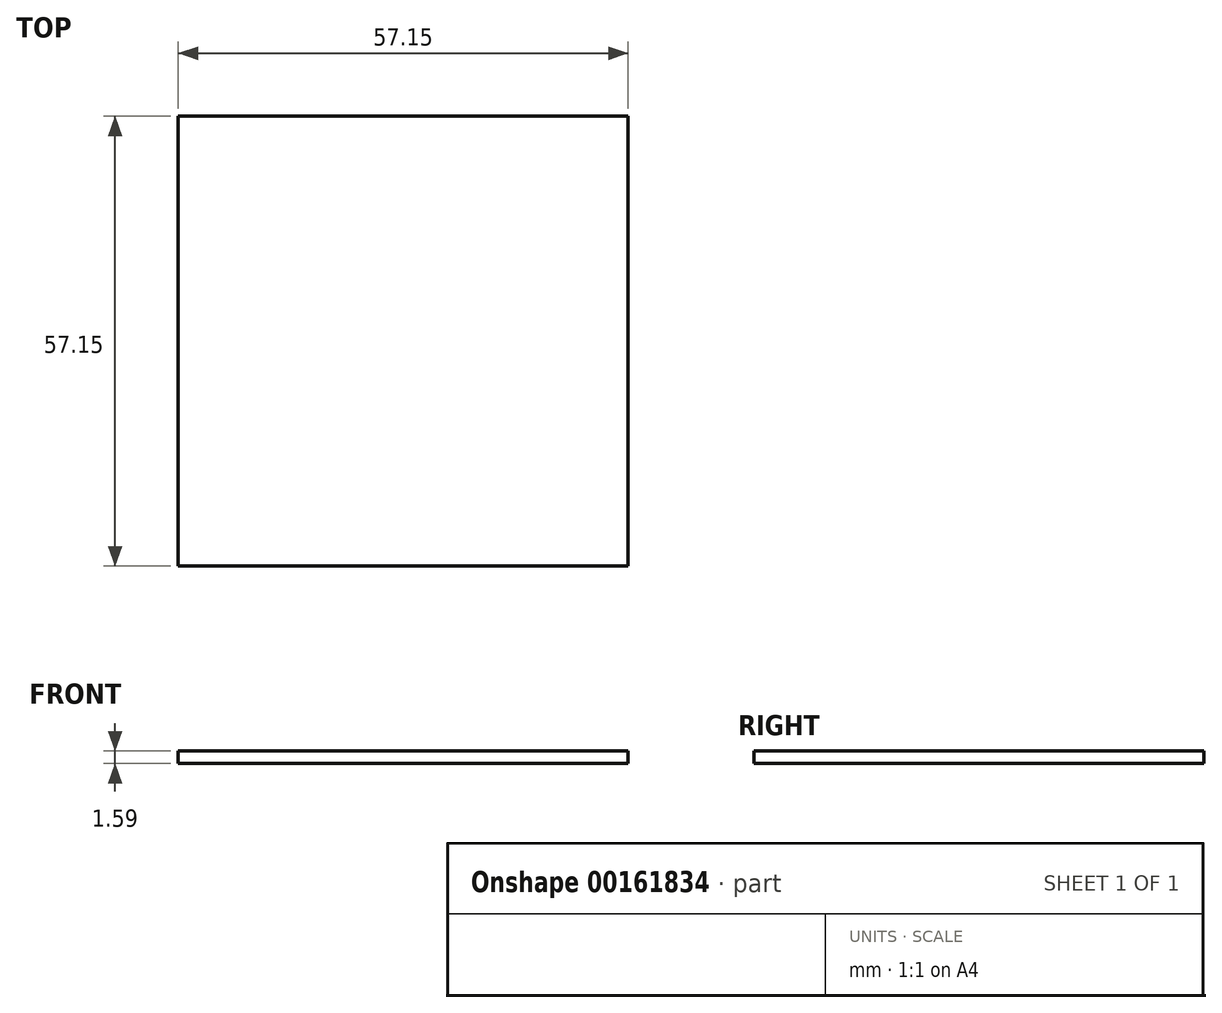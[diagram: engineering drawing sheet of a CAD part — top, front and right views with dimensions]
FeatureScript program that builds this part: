
annotation { "Feature Type Name" : "Feature", "Feature Type Description" : "" }
export const myFeature = defineFeature(function(context is Context, id is Id, definition is map)
    precondition{}
    {
        {
            var Q0;
            Q0=qCreatedBy(makeId("Top.planeOp"),FACE);
            var sketch = newSketch(context, id + "F0", { "sketchPlane" : qUnion([Q0])});
            skLineSegment(sketch, "E0", {"start": v(39.69, 57.15) * mm, "end": v(39.69, 0) * mm});
            skLineSegment(sketch, "E1", {"start": v(39.69, 0) * mm, "end": v(96.84, 0) * mm});
            skLineSegment(sketch, "E2", {"start": v(96.84, 0) * mm, "end": v(96.84, 57.15) * mm});
            skLineSegment(sketch, "E3.top", {"start": v(39.69, 57.15) * mm, "end": v(96.84, 57.15) * mm});
            skLineSegment(sketch, "E3.left", {"start": v(39.69, 0) * mm, "end": v(39.69, 57.15) * mm});
            skSolve(sketch);
        }
        {
            var Q0;
            Q0=qSketchRegion(id+"F0",true);
            extrude(context, id + "F1", {"entities" : qUnion([Q0]), "depth" : 1.59 * mm});
        }
    });
